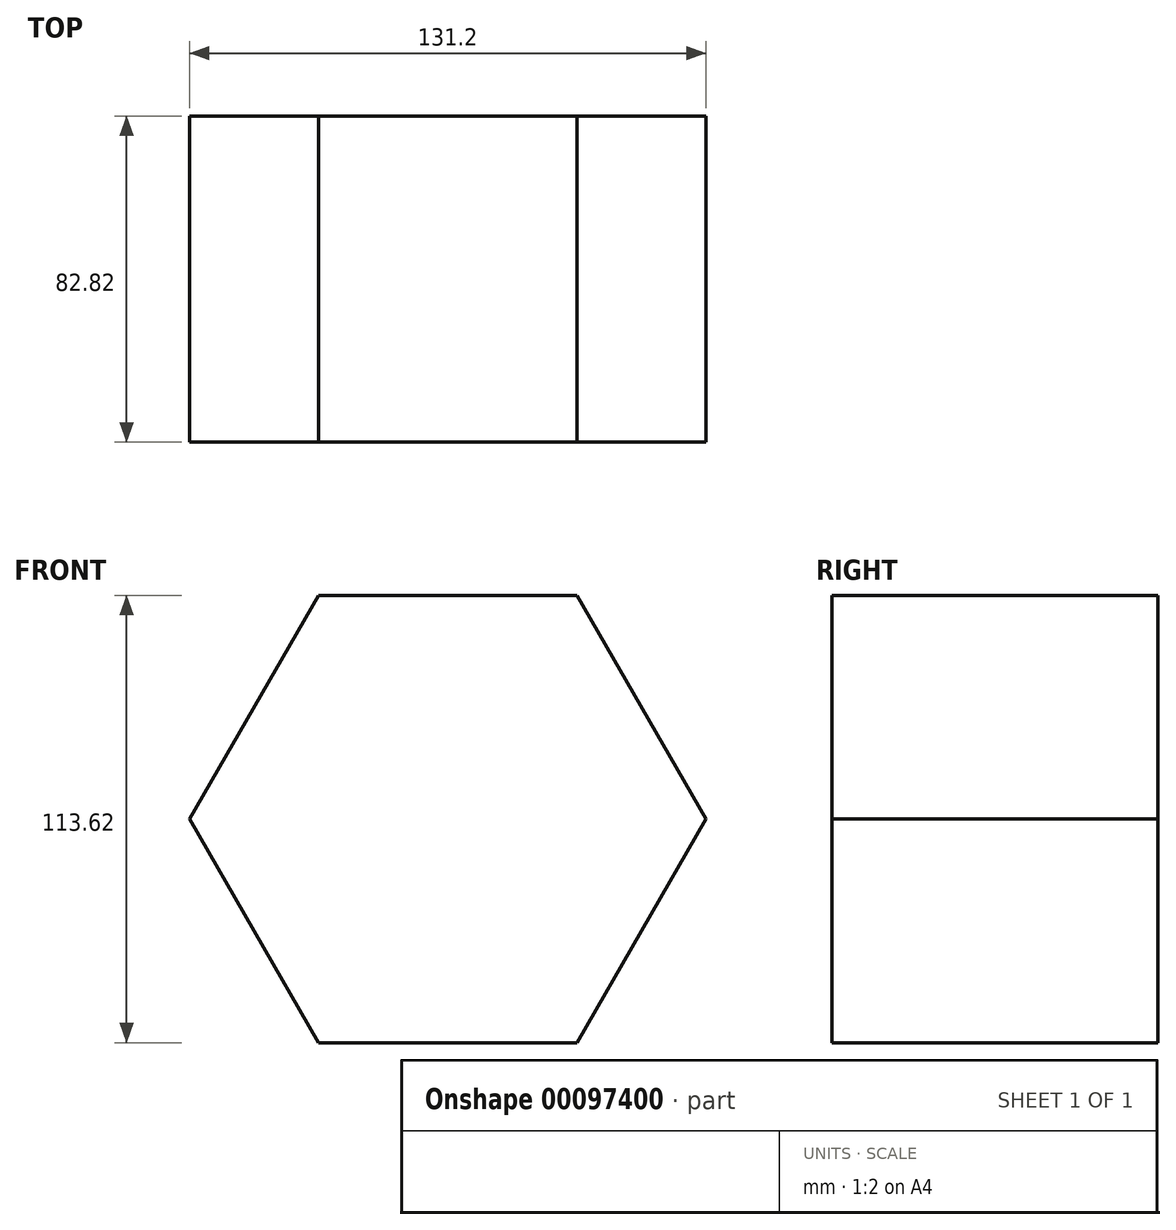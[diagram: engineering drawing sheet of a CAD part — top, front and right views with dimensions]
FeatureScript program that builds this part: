
annotation { "Feature Type Name" : "Feature", "Feature Type Description" : "" }
export const myFeature = defineFeature(function(context is Context, id is Id, definition is map)
    precondition{}
    {
        {
            var Q0;
            Q0=qCreatedBy(makeId("Front.planeOp"),FACE);
            var sketch = newSketch(context, id + "F0", { "sketchPlane" : qUnion([Q0])});
            skCircle(sketch, "E0.cCircle", {"center": v(0, 0) * mm, "radius": 56.8 * mm, "construction": true});
            skLineSegment(sketch, "E0.0", {"start": v(-32.8, 56.8) * mm, "end": v(32.8, 56.8) * mm});
            skLineSegment(sketch, "E0.1", {"start": v(32.8, 56.8) * mm, "end": v(65.6, 0) * mm});
            skLineSegment(sketch, "E0.2", {"start": v(65.6, 0) * mm, "end": v(32.8, -56.8) * mm});
            skLineSegment(sketch, "E0.3", {"start": v(32.8, -56.8) * mm, "end": v(-32.8, -56.8) * mm});
            skLineSegment(sketch, "E0.4", {"start": v(-32.8, -56.8) * mm, "end": v(-65.6, 0) * mm});
            skLineSegment(sketch, "E0.5", {"start": v(-65.6, 0) * mm, "end": v(-32.8, 56.8) * mm});
            skPoint(sketch, "E0.0.midPoint", {"position": v(0, 56.8) * mm});
            skSolve(sketch);
        }
        {
            var Q0;
            Q0 = qSketchRegion(id + "F0", true);
            extrude(context, id + "F1", {"entities" : qUnion([Q0]), "depth" : 82.82 * mm});
        }
    });
